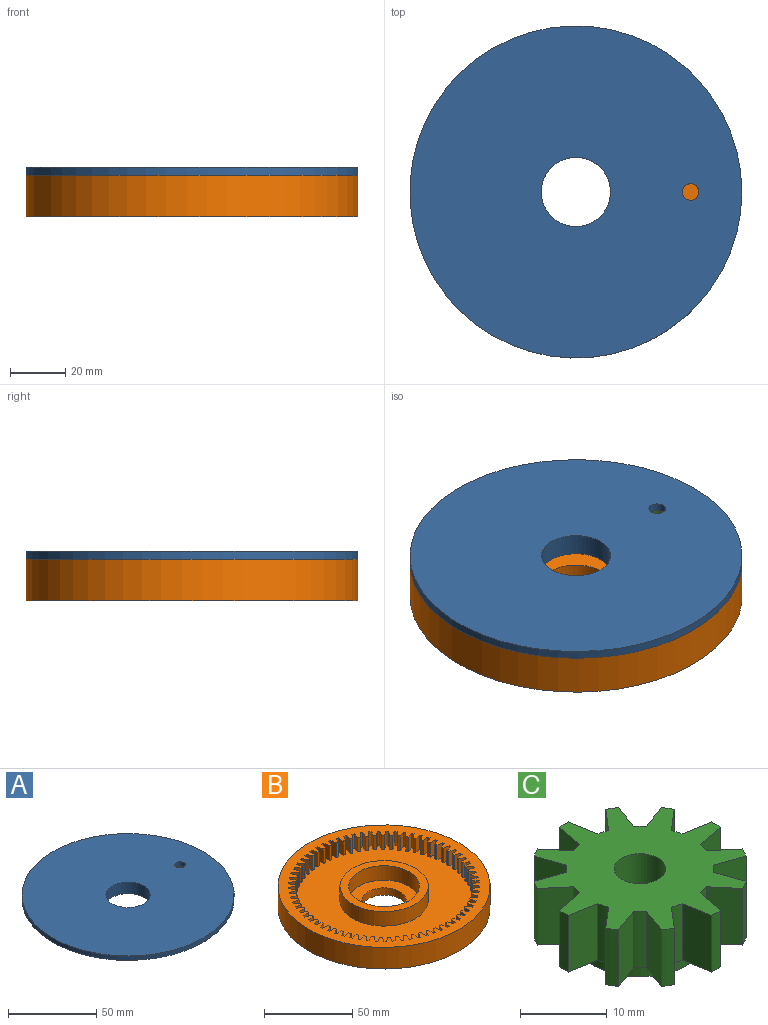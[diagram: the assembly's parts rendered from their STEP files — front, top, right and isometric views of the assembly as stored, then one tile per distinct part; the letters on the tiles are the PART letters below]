
ASSEMBLY  parts=3 mates=2
PART A: 7 faces, bbox 120x120x8 mm
  f0: cylinder r=19.5mm len=39mm, axis (0,0,-1), area 612.6mm2, adj f1,f4
  f1: plane 39x39mm, normal (0,0,-1), area 703.7mm2, adj f0,f5
  f2: cylinder r=60mm len=120mm, axis (0,0,-1), area 1131mm2, adj f3,f4
  f3: plane 120x120mm, normal (0,0,1), area 10790.6mm2, adj f2,f5,f6
  f4: plane 120x120mm, normal (0,0,-1), area 10086.9mm2, adj f0,f2,f6
  f5: cylinder r=12.5mm len=25mm, axis (0,0,1), area 628.3mm2, adj f1,f3
  f6: cylinder r=3mm len=6mm, axis (0,0,1), area 56.5mm2, adj f3,f4
PART B: 285 faces, bbox 120x120x15 mm
  f0: cylinder r=50mm len=10mm, axis (0,0,-1), area 15.5mm2, adj f69,f71,f277,f282
  f1: cylinder r=50mm len=10mm, axis (0,0,-1), area 15.5mm2, adj f69,f71,f274,f279
  f2: cylinder r=50mm len=10mm, axis (0,0,-1), area 15.5mm2, adj f69,f71,f271,f276
  f3: cylinder r=50mm len=10mm, axis (0,0,-1), area 15.5mm2, adj f69,f71,f268,f273
  f4: cylinder r=50mm len=10mm, axis (0,0,-1), area 15.5mm2, adj f69,f71,f265,f270
  f5: cylinder r=50mm len=10mm, axis (0,0,-1), area 15.5mm2, adj f69,f71,f262,f267
  f6: cylinder r=50mm len=10mm, axis (0,0,-1), area 15.5mm2, adj f69,f71,f259,f264
  f7: cylinder r=50mm len=10mm, axis (0,0,-1), area 15.5mm2, adj f69,f71,f235,f261
  f8: cylinder r=50mm len=10mm, axis (0,0,-1), area 15.5mm2, adj f69,f71,f247,f258
  f9: cylinder r=50mm len=10mm, axis (0,0,-1), area 15.5mm2, adj f69,f71,f255,f256
  f10: cylinder r=50mm len=10mm, axis (0,0,-1), area 15.5mm2, adj f69,f71,f232,f252
  f11: cylinder r=50mm len=10mm, axis (0,0,-1), area 15.5mm2, adj f69,f71,f249,f250
  f12: cylinder r=50mm len=10mm, axis (0,0,-1), area 15.5mm2, adj f69,f71,f241,f246
  f13: cylinder r=50mm len=10mm, axis (0,0,-1), area 15.5mm2, adj f69,f71,f243,f253
  f14: cylinder r=50mm len=10mm, axis (0,0,-1), area 15.5mm2, adj f69,f71,f240,f244
  f15: cylinder r=50mm len=10mm, axis (0,0,-1), area 15.5mm2, adj f69,f71,f237,f238
  f16: cylinder r=50mm len=10mm, axis (0,0,-1), area 15.5mm2, adj f69,f71,f229,f234
  f17: cylinder r=50mm len=10mm, axis (0,0,-1), area 15.5mm2, adj f69,f71,f226,f231
  f18: cylinder r=50mm len=10mm, axis (0,0,-1), area 15.5mm2, adj f69,f71,f223,f228
  f19: cylinder r=50mm len=10mm, axis (0,0,-1), area 15.5mm2, adj f69,f71,f220,f225
  f20: cylinder r=50mm len=10mm, axis (0,0,-1), area 15.5mm2, adj f69,f71,f217,f222
  f21: cylinder r=50mm len=10mm, axis (0,0,-1), area 15.5mm2, adj f69,f71,f214,f219
  f22: cylinder r=50mm len=10mm, axis (0,0,-1), area 15.5mm2, adj f69,f71,f211,f216
  f23: cylinder r=50mm len=10mm, axis (0,0,-1), area 15.5mm2, adj f69,f71,f208,f213
  f24: cylinder r=50mm len=10mm, axis (0,0,-1), area 15.5mm2, adj f69,f71,f205,f210
  f25: cylinder r=50mm len=10mm, axis (0,0,-1), area 15.5mm2, adj f69,f71,f202,f207
  f26: cylinder r=50mm len=10mm, axis (0,0,-1), area 15.5mm2, adj f69,f71,f199,f204
  f27: cylinder r=50mm len=10mm, axis (0,0,-1), area 15.5mm2, adj f69,f71,f190,f201
  f28: cylinder r=50mm len=10mm, axis (0,0,-1), area 15.5mm2, adj f69,f71,f193,f198
  f29: cylinder r=50mm len=10mm, axis (0,0,-1), area 15.5mm2, adj f69,f71,f94,f195
  f30: cylinder r=50mm len=10mm, axis (0,0,-1), area 15.5mm2, adj f69,f71,f187,f192
  f31: cylinder r=50mm len=10mm, axis (0,0,-1), area 15.5mm2, adj f69,f71,f189,f196
  f32: cylinder r=50mm len=10mm, axis (0,0,-1), area 15.5mm2, adj f69,f71,f181,f186
  f33: cylinder r=50mm len=10mm, axis (0,0,-1), area 15.5mm2, adj f69,f71,f76,f183
  f34: cylinder r=50mm len=10mm, axis (0,0,-1), area 15.5mm2, adj f69,f71,f180,f184
  f35: cylinder r=50mm len=10mm, axis (0,0,-1), area 15.5mm2, adj f69,f71,f177,f178
  f36: cylinder r=50mm len=10mm, axis (0,0,-1), area 15.5mm2, adj f69,f71,f174,f175
  f37: cylinder r=50mm len=10mm, axis (0,0,-1), area 15.5mm2, adj f69,f71,f171,f172
  f38: cylinder r=50mm len=10mm, axis (0,0,-1), area 15.5mm2, adj f69,f71,f168,f169
  f39: cylinder r=50mm len=10mm, axis (0,0,-1), area 15.5mm2, adj f69,f71,f164,f166
  f40: cylinder r=50mm len=10mm, axis (0,0,-1), area 15.5mm2, adj f69,f71,f162,f165
  f41: cylinder r=50mm len=10mm, axis (0,0,-1), area 15.5mm2, adj f69,f71,f159,f160
  f42: cylinder r=50mm len=10mm, axis (0,0,-1), area 15.5mm2, adj f69,f71,f156,f157
  f43: cylinder r=50mm len=10mm, axis (0,0,-1), area 15.5mm2, adj f69,f71,f153,f154
  f44: cylinder r=50mm len=10mm, axis (0,0,-1), area 15.5mm2, adj f69,f71,f142,f150
  f45: cylinder r=50mm len=10mm, axis (0,0,-1), area 15.5mm2, adj f69,f71,f147,f148
  f46: cylinder r=50mm len=10mm, axis (0,0,-1), area 15.5mm2, adj f69,f71,f139,f144
  f47: cylinder r=50mm len=10mm, axis (0,0,-1), area 15.5mm2, adj f69,f71,f141,f151
  f48: cylinder r=50mm len=10mm, axis (0,0,-1), area 15.5mm2, adj f69,f71,f133,f138
  f49: cylinder r=50mm len=10mm, axis (0,0,-1), area 15.5mm2, adj f69,f71,f127,f135
  f50: cylinder r=50mm len=10mm, axis (0,0,-1), area 15.5mm2, adj f69,f71,f132,f145
  f51: cylinder r=50mm len=10mm, axis (0,0,-1), area 15.5mm2, adj f69,f71,f129,f130
  f52: cylinder r=50mm len=10mm, axis (0,0,-1), area 15.5mm2, adj f69,f71,f126,f136
  f53: cylinder r=50mm len=10mm, axis (0,0,-1), area 15.5mm2, adj f69,f71,f123,f124
  f54: cylinder r=50mm len=10mm, axis (0,0,-1), area 15.5mm2, adj f69,f71,f120,f121
  f55: cylinder r=50mm len=10mm, axis (0,0,-1), area 15.5mm2, adj f69,f71,f117,f118
  f56: cylinder r=50mm len=10mm, axis (0,0,-1), area 15.5mm2, adj f69,f71,f114,f115
  f57: cylinder r=50mm len=10mm, axis (0,0,-1), area 15.5mm2, adj f69,f71,f111,f112
  f58: cylinder r=50mm len=10mm, axis (0,0,-1), area 15.5mm2, adj f69,f71,f108,f109
  f59: cylinder r=50mm len=10mm, axis (0,0,-1), area 15.5mm2, adj f69,f71,f105,f106
  f60: cylinder r=50mm len=10mm, axis (0,0,-1), area 15.5mm2, adj f69,f71,f102,f103
  f61: cylinder r=50mm len=10mm, axis (0,0,-1), area 15.5mm2, adj f69,f71,f99,f100
  f62: cylinder r=50mm len=10mm, axis (0,0,-1), area 15.5mm2, adj f69,f71,f91,f96
  f63: cylinder r=50mm len=10mm, axis (0,0,-1), area 15.5mm2, adj f69,f71,f93,f97
  f64: cylinder r=50mm len=10mm, axis (0,0,-1), area 15.5mm2, adj f69,f71,f82,f90
  f65: cylinder r=50mm len=10mm, axis (0,0,-1), area 15.5mm2, adj f69,f71,f87,f88
  f66: cylinder r=50mm len=10mm, axis (0,0,-1), area 15.5mm2, adj f69,f71,f79,f84
  f67: cylinder r=50mm len=10mm, axis (0,0,-1), area 15.5mm2, adj f69,f71,f81,f280
  f68: cylinder r=50mm len=10mm, axis (0,0,-1), area 15.5mm2, adj f69,f71,f78,f85
  f69: plane 120x120mm, normal (0,0,1), area 2834.4mm2, adj f0,f1,f2,f3,f4,f5,f6,f7
  f70: plane 120x120mm, normal (0,0,-1), area 10818.9mm2, adj f283,f284
  f71: plane 108.01x107.98mm, normal (0,0,1), area 6511.9mm2, adj f0,f1,f2,f3,f4,f5,f6,f7
  f72: cylinder r=20mm len=40mm, axis (0,0,-1), area 1256.6mm2, adj f74,f75
  f73: cylinder r=25mm len=50mm, axis (0,0,-1), area 1570.8mm2, adj f71,f74
  f74: plane 50x50mm, normal (0,0,1), area 706.9mm2, adj f72,f73
  f75: plane 40x40mm, normal (0,0,1), area 765.8mm2, adj f72,f283
  f76: plane 10x3.24mm, normal (-0.61,-0.79,0), area 40.9mm2, adj f33,f69,f71,f77
  f77: plane 10x1.12mm, normal (0.67,-0.75,0), area 15mm2, adj f69,f71,f76,f78
  f78: plane 10x3.5mm, normal (0.86,0.52,0), area 40.9mm2, adj f68,f69,f71,f77
  f79: plane 10x3.92mm, normal (-0.29,-0.96,0), area 40.9mm2, adj f66,f69,f71,f80
  f80: plane 10x1.33mm, normal (0.89,-0.46,0), area 15mm2, adj f69,f71,f79,f81
  f81: plane 10x3.23mm, normal (0.62,0.79,0), area 40.9mm2, adj f67,f69,f71,f80
  f82: plane 10x3.79mm, normal (-0.38,-0.93,0), area 40.9mm2, adj f64,f69,f71,f83
  f83: plane 10x1.26mm, normal (0.84,-0.54,0), area 15mm2, adj f69,f71,f82,f84
  f84: plane 10x2.98mm, normal (0.68,0.73,0), area 40.9mm2, adj f66,f69,f71,f83
  f85: plane 10x3.45mm, normal (-0.54,-0.84,0), area 40.9mm2, adj f68,f69,f71,f86
  f86: plane 10x1.1mm, normal (0.73,-0.68,0), area 15mm2, adj f69,f71,f85,f87
  f87: plane 10x3.29mm, normal (0.8,0.59,0), area 40.9mm2, adj f65,f69,f71,f86
  f88: plane 10x3.64mm, normal (-0.46,-0.89,0), area 40.9mm2, adj f65,f69,f71,f89
  f89: plane 10x1.19mm, normal (0.79,-0.61,0), area 15mm2, adj f69,f71,f88,f90
  f90: plane 10x3.06mm, normal (0.75,0.66,0), area 40.9mm2, adj f64,f69,f71,f89
  f91: plane 10x3.86mm, normal (0.33,0.94,0), area 40.9mm2, adj f62,f69,f71,f92
  f92: plane 10x1.3mm, normal (-0.87,0.5,0), area 15mm2, adj f69,f71,f91,f93
  f93: plane 10x3.11mm, normal (-0.65,-0.76,0), area 40.9mm2, adj f63,f69,f71,f92
  f94: plane 10x3.72mm, normal (0.42,0.91,0), area 40.9mm2, adj f29,f69,f71,f95
  f95: plane 10x1.23mm, normal (-0.82,0.58,0), area 15mm2, adj f69,f71,f94,f96
  f96: plane 10x2.93mm, normal (-0.72,-0.7,0), area 40.9mm2, adj f62,f69,f71,f95
  f97: plane 10x3.97mm, normal (0.25,0.97,0), area 40.9mm2, adj f63,f69,f71,f98
  f98: plane 10x1.36mm, normal (-0.91,0.42,0), area 15mm2, adj f69,f71,f97,f99
  f99: plane 10x3.34mm, normal (-0.58,-0.82,0), area 40.9mm2, adj f61,f69,f71,f98
  f100: plane 10x4.04mm, normal (0.16,0.99,0), area 40.9mm2, adj f61,f69,f71,f101
  f101: plane 10x1.41mm, normal (-0.94,0.33,0), area 15mm2, adj f69,f71,f100,f102
  f102: plane 10x3.54mm, normal (-0.5,-0.86,0), area 40.9mm2, adj f60,f69,f71,f101
  f103: plane 10x4.08mm, normal (0.07,1,0), area 40.9mm2, adj f60,f69,f71,f104
  f104: plane 10x1.45mm, normal (-0.97,0.25,0), area 15mm2, adj f69,f71,f103,f105
  f105: plane 10x3.71mm, normal (-0.42,-0.91,0), area 40.9mm2, adj f59,f69,f71,f104
  f106: plane 10x4.09mm, normal (-0.02,1,0), area 40.9mm2, adj f59,f69,f71,f107
  f107: plane 10x1.48mm, normal (-0.99,0.16,0), area 15mm2, adj f69,f71,f106,f108
  f108: plane 10x3.85mm, normal (-0.34,-0.94,0), area 40.9mm2, adj f58,f69,f71,f107
  f109: plane 10x4.06mm, normal (-0.12,0.99,0), area 40.9mm2, adj f58,f69,f71,f110
  f110: plane 10x1.5mm, normal (-1,0.07,0), area 15mm2, adj f69,f71,f109,f111
  f111: plane 10x3.96mm, normal (-0.25,-0.97,0), area 40.9mm2, adj f57,f69,f71,f110
  f112: plane 10x4mm, normal (-0.21,0.98,0), area 40.9mm2, adj f57,f69,f71,f113
  f113: plane 10x1.5mm, normal (-1,-0.02,0), area 15mm2, adj f69,f71,f112,f114
  f114: plane 10x4.04mm, normal (-0.16,-0.99,0), area 40.9mm2, adj f56,f69,f71,f113
  f115: plane 10x3.91mm, normal (-0.29,0.96,0), area 40.9mm2, adj f56,f69,f71,f116
  f116: plane 10x1.49mm, normal (-0.99,-0.11,0), area 15mm2, adj f69,f71,f115,f117
  f117: plane 10x4.08mm, normal (-0.07,-1,0), area 40.9mm2, adj f55,f69,f71,f116
  f118: plane 10x3.79mm, normal (-0.38,0.93,0), area 40.9mm2, adj f55,f69,f71,f119
  f119: plane 10x1.47mm, normal (-0.98,-0.2,0), area 15mm2, adj f69,f71,f118,f120
  f120: plane 10x4.09mm, normal (0.02,-1,0), area 40.9mm2, adj f54,f69,f71,f119
  f121: plane 10x3.63mm, normal (-0.46,0.89,0), area 40.9mm2, adj f54,f69,f71,f122
  f122: plane 10x1.43mm, normal (-0.96,-0.29,0), area 15mm2, adj f69,f71,f121,f123
  f123: plane 10x4.07mm, normal (0.11,-0.99,0), area 40.9mm2, adj f53,f69,f71,f122
  f124: plane 10x3.44mm, normal (-0.54,0.84,0), area 40.9mm2, adj f53,f69,f71,f125
  f125: plane 10x1.39mm, normal (-0.93,-0.38,0), area 15mm2, adj f69,f71,f124,f126
  f126: plane 10x4.01mm, normal (0.2,-0.98,0), area 40.9mm2, adj f52,f69,f71,f125
  f127: plane 10x3.06mm, normal (-0.75,0.66,0), area 40.9mm2, adj f49,f69,f71,f128
  f128: plane 10x1.19mm, normal (-0.79,-0.61,0), area 15mm2, adj f69,f71,f127,f129
  f129: plane 10x3.64mm, normal (0.46,-0.89,0), area 40.9mm2, adj f51,f69,f71,f128
  f130: plane 10x3.29mm, normal (-0.8,0.59,0), area 40.9mm2, adj f51,f69,f71,f131
  f131: plane 10x1.1mm, normal (-0.73,-0.68,0), area 15mm2, adj f69,f71,f130,f132
  f132: plane 10x3.45mm, normal (0.54,-0.84,0), area 40.9mm2, adj f50,f69,f71,f131
  f133: plane 10x2.98mm, normal (-0.68,0.73,0), area 40.9mm2, adj f48,f69,f71,f134
  f134: plane 10x1.26mm, normal (-0.84,-0.54,0), area 15mm2, adj f69,f71,f133,f135
  f135: plane 10x3.79mm, normal (0.38,-0.93,0), area 40.9mm2, adj f49,f69,f71,f134
  f136: plane 10x3.23mm, normal (-0.62,0.79,0), area 40.9mm2, adj f52,f69,f71,f137
  f137: plane 10x1.33mm, normal (-0.89,-0.46,0), area 15mm2, adj f69,f71,f136,f138
  f138: plane 10x3.92mm, normal (0.29,-0.96,0), area 40.9mm2, adj f48,f69,f71,f137
  f139: plane 10x3.94mm, normal (-0.96,0.27,0), area 40.9mm2, adj f46,f69,f71,f140
  f140: plane 10x1.35mm, normal (-0.44,-0.9,0), area 15mm2, adj f69,f71,f139,f141
  f141: plane 10x3.28mm, normal (0.8,-0.6,0), area 40.9mm2, adj f47,f69,f71,f140
  f142: plane 10x3.83mm, normal (-0.94,0.35,0), area 40.9mm2, adj f44,f69,f71,f143
  f143: plane 10x1.28mm, normal (-0.52,-0.85,0), area 15mm2, adj f69,f71,f142,f144
  f144: plane 10x3.05mm, normal (0.74,-0.67,0), area 40.9mm2, adj f46,f69,f71,f143
  f145: plane 10x3.5mm, normal (-0.86,0.52,0), area 40.9mm2, adj f50,f69,f71,f146
  f146: plane 10x1.12mm, normal (-0.67,-0.75,0), area 15mm2, adj f69,f71,f145,f147
  f147: plane 10x3.24mm, normal (0.61,-0.79,0), area 40.9mm2, adj f45,f69,f71,f146
  f148: plane 10x3.68mm, normal (-0.9,0.44,0), area 40.9mm2, adj f45,f69,f71,f149
  f149: plane 10x1.21mm, normal (-0.6,-0.8,0), area 15mm2, adj f69,f71,f148,f150
  f150: plane 10x3mm, normal (0.68,-0.73,0), area 40.9mm2, adj f44,f69,f71,f149
  f151: plane 10x4.03mm, normal (-0.98,0.18,0), area 40.9mm2, adj f47,f69,f71,f152
  f152: plane 10x1.4mm, normal (-0.36,-0.93,0), area 15mm2, adj f69,f71,f151,f153
  f153: plane 10x3.49mm, normal (0.85,-0.52,0), area 40.9mm2, adj f43,f69,f71,f152
  f154: plane 10x4.08mm, normal (-1,0.09,0), area 40.9mm2, adj f43,f69,f71,f155
  f155: plane 10x1.44mm, normal (-0.27,-0.96,0), area 15mm2, adj f69,f71,f154,f156
  f156: plane 10x3.67mm, normal (0.9,-0.44,0), area 40.9mm2, adj f42,f69,f71,f155
  f157: plane 10x4.09mm, normal (-1,0,0), area 40.9mm2, adj f42,f69,f71,f158
  f158: plane 10x1.48mm, normal (-0.18,-0.98,0), area 15mm2, adj f69,f71,f157,f159
  f159: plane 10x3.82mm, normal (0.93,-0.36,0), area 40.9mm2, adj f41,f69,f71,f158
  f160: plane 10x4.07mm, normal (-1,-0.09,0), area 40.9mm2, adj f41,f69,f71,f161
  f161: plane 10x1.49mm, normal (-0.09,-1,0), area 15mm2, adj f69,f71,f160,f162
  f162: plane 10x3.94mm, normal (0.96,-0.27,0), area 40.9mm2, adj f40,f69,f71,f161
  f163: plane 10x1.5mm, normal (0,-1,0), area 15mm2, adj f69,f71,f164,f165
  f164: plane 10x4.02mm, normal (0.98,-0.18,0), area 40.9mm2, adj f39,f69,f71,f163
  f165: plane 10x4.02mm, normal (-0.98,-0.18,0), area 40.9mm2, adj f40,f69,f71,f163
  f166: plane 10x3.94mm, normal (-0.96,-0.27,0), area 40.9mm2, adj f39,f69,f71,f167
  f167: plane 10x1.49mm, normal (0.09,-1,0), area 15mm2, adj f69,f71,f166,f168
  f168: plane 10x4.07mm, normal (1,-0.09,0), area 40.9mm2, adj f38,f69,f71,f167
  f169: plane 10x3.82mm, normal (-0.93,-0.36,0), area 40.9mm2, adj f38,f69,f71,f170
  f170: plane 10x1.48mm, normal (0.18,-0.98,0), area 15mm2, adj f69,f71,f169,f171
  f171: plane 10x4.09mm, normal (1,0,0), area 40.9mm2, adj f37,f69,f71,f170
  f172: plane 10x3.67mm, normal (-0.9,-0.44,0), area 40.9mm2, adj f37,f69,f71,f173
  f173: plane 10x1.44mm, normal (0.27,-0.96,0), area 15mm2, adj f69,f71,f172,f174
  f174: plane 10x4.08mm, normal (1,0.09,0), area 40.9mm2, adj f36,f69,f71,f173
  f175: plane 10x3.49mm, normal (-0.85,-0.52,0), area 40.9mm2, adj f36,f69,f71,f176
  f176: plane 10x1.4mm, normal (0.36,-0.93,0), area 15mm2, adj f69,f71,f175,f177
  f177: plane 10x4.03mm, normal (0.98,0.18,0), area 40.9mm2, adj f35,f69,f71,f176
  f178: plane 10x3.28mm, normal (-0.8,-0.6,0), area 40.9mm2, adj f35,f69,f71,f179
  f179: plane 10x1.35mm, normal (0.44,-0.9,0), area 15mm2, adj f69,f71,f178,f180
  f180: plane 10x3.94mm, normal (0.96,0.27,0), area 40.9mm2, adj f34,f69,f71,f179
  f181: plane 10x3mm, normal (-0.68,-0.73,0), area 40.9mm2, adj f32,f69,f71,f182
  f182: plane 10x1.21mm, normal (0.6,-0.8,0), area 15mm2, adj f69,f71,f181,f183
  f183: plane 10x3.68mm, normal (0.9,0.44,0), area 40.9mm2, adj f33,f69,f71,f182
  f184: plane 10x3.05mm, normal (-0.74,-0.67,0), area 40.9mm2, adj f34,f69,f71,f185
  f185: plane 10x1.28mm, normal (0.52,-0.85,0), area 15mm2, adj f69,f71,f184,f186
  f186: plane 10x3.83mm, normal (0.94,0.35,0), area 40.9mm2, adj f32,f69,f71,f185
  f187: plane 10x3.12mm, normal (0.65,0.76,0), area 40.9mm2, adj f30,f69,f71,f188
  f188: plane 10x1.16mm, normal (-0.63,0.78,0), area 15mm2, adj f69,f71,f187,f189
  f189: plane 10x3.59mm, normal (-0.88,-0.48,0), area 40.9mm2, adj f31,f69,f71,f188
  f190: plane 10x2.92mm, normal (0.71,0.7,0), area 40.9mm2, adj f27,f69,f71,f191
  f191: plane 10x1.25mm, normal (-0.56,0.83,0), area 15mm2, adj f69,f71,f190,f192
  f192: plane 10x3.76mm, normal (-0.92,-0.4,0), area 40.9mm2, adj f30,f69,f71,f191
  f193: plane 10x3.55mm, normal (0.5,0.87,0), area 40.9mm2, adj f28,f69,f71,f194
  f194: plane 10x1.14mm, normal (-0.76,0.65,0), area 15mm2, adj f69,f71,f193,f195
  f195: plane 10x3.18mm, normal (-0.78,-0.63,0), area 40.9mm2, adj f29,f69,f71,f194
  f196: plane 10x3.35mm, normal (0.57,0.82,0), area 40.9mm2, adj f31,f69,f71,f197
  f197: plane 10x1.07mm, normal (-0.7,0.72,0), area 15mm2, adj f69,f71,f196,f198
  f198: plane 10x3.4mm, normal (-0.83,-0.56,0), area 40.9mm2, adj f28,f69,f71,f197
  f199: plane 10x3.17mm, normal (0.77,0.63,0), area 40.9mm2, adj f26,f69,f71,f200
  f200: plane 10x1.32mm, normal (-0.48,0.88,0), area 15mm2, adj f69,f71,f199,f201
  f201: plane 10x3.89mm, normal (-0.95,-0.31,0), area 40.9mm2, adj f27,f69,f71,f200
  f202: plane 10x3.39mm, normal (0.83,0.56,0), area 40.9mm2, adj f25,f69,f71,f203
  f203: plane 10x1.38mm, normal (-0.4,0.92,0), area 15mm2, adj f69,f71,f202,f204
  f204: plane 10x3.99mm, normal (-0.97,-0.22,0), area 40.9mm2, adj f26,f69,f71,f203
  f205: plane 10x3.59mm, normal (0.88,0.48,0), area 40.9mm2, adj f24,f69,f71,f206
  f206: plane 10x1.42mm, normal (-0.31,0.95,0), area 15mm2, adj f69,f71,f205,f207
  f207: plane 10x4.06mm, normal (-0.99,-0.13,0), area 40.9mm2, adj f25,f69,f71,f206
  f208: plane 10x3.75mm, normal (0.92,0.4,0), area 40.9mm2, adj f23,f69,f71,f209
  f209: plane 10x1.46mm, normal (-0.23,0.97,0), area 15mm2, adj f69,f71,f208,f210
  f210: plane 10x4.09mm, normal (-1,-0.04,0), area 40.9mm2, adj f24,f69,f71,f209
  f211: plane 10x3.88mm, normal (0.95,0.32,0), area 40.9mm2, adj f22,f69,f71,f212
  f212: plane 10x1.49mm, normal (-0.14,0.99,0), area 15mm2, adj f69,f71,f211,f213
  f213: plane 10x4.09mm, normal (-1,0.05,0), area 40.9mm2, adj f23,f69,f71,f212
  f214: plane 10x3.98mm, normal (0.97,0.23,0), area 40.9mm2, adj f21,f69,f71,f215
  f215: plane 10x1.5mm, normal (-0.05,1,0), area 15mm2, adj f69,f71,f214,f216
  f216: plane 10x4.05mm, normal (-0.99,0.14,0), area 40.9mm2, adj f22,f69,f71,f215
  f217: plane 10x4.05mm, normal (0.99,0.14,0), area 40.9mm2, adj f20,f69,f71,f218
  f218: plane 10x1.5mm, normal (0.05,1,0), area 15mm2, adj f69,f71,f217,f219
  f219: plane 10x3.98mm, normal (-0.97,0.23,0), area 40.9mm2, adj f21,f69,f71,f218
  f220: plane 10x4.09mm, normal (1,0.05,0), area 40.9mm2, adj f19,f69,f71,f221
  f221: plane 10x1.49mm, normal (0.14,0.99,0), area 15mm2, adj f69,f71,f220,f222
  f222: plane 10x3.88mm, normal (-0.95,0.32,0), area 40.9mm2, adj f20,f69,f71,f221
  f223: plane 10x4.09mm, normal (1,-0.04,0), area 40.9mm2, adj f18,f69,f71,f224
  f224: plane 10x1.46mm, normal (0.23,0.97,0), area 15mm2, adj f69,f71,f223,f225
  f225: plane 10x3.75mm, normal (-0.92,0.4,0), area 40.9mm2, adj f19,f69,f71,f224
  f226: plane 10x4.06mm, normal (0.99,-0.13,0), area 40.9mm2, adj f17,f69,f71,f227
  f227: plane 10x1.42mm, normal (0.31,0.95,0), area 15mm2, adj f69,f71,f226,f228
  f228: plane 10x3.59mm, normal (-0.88,0.48,0), area 40.9mm2, adj f18,f69,f71,f227
  f229: plane 10x3.99mm, normal (0.97,-0.22,0), area 40.9mm2, adj f16,f69,f71,f230
  f230: plane 10x1.38mm, normal (0.4,0.92,0), area 15mm2, adj f69,f71,f229,f231
  f231: plane 10x3.39mm, normal (-0.83,0.56,0), area 40.9mm2, adj f17,f69,f71,f230
  f232: plane 10x3.89mm, normal (0.95,-0.31,0), area 40.9mm2, adj f10,f69,f71,f233
  f233: plane 10x1.32mm, normal (0.48,0.88,0), area 15mm2, adj f69,f71,f232,f234
  f234: plane 10x3.17mm, normal (-0.77,0.63,0), area 40.9mm2, adj f16,f69,f71,f233
  f235: plane 10x3.54mm, normal (0.5,-0.86,0), area 40.9mm2, adj f7,f69,f71,f236
  f236: plane 10x1.41mm, normal (0.94,0.33,0), area 15mm2, adj f69,f71,f235,f237
  f237: plane 10x4.04mm, normal (-0.16,0.99,0), area 40.9mm2, adj f15,f69,f71,f236
  f238: plane 10x3.34mm, normal (0.58,-0.82,0), area 40.9mm2, adj f15,f69,f71,f239
  f239: plane 10x1.36mm, normal (0.91,0.42,0), area 15mm2, adj f69,f71,f238,f240
  f240: plane 10x3.97mm, normal (-0.25,0.97,0), area 40.9mm2, adj f14,f69,f71,f239
  f241: plane 10x2.93mm, normal (0.72,-0.7,0), area 40.9mm2, adj f12,f69,f71,f242
  f242: plane 10x1.23mm, normal (0.82,0.58,0), area 15mm2, adj f69,f71,f241,f243
  f243: plane 10x3.72mm, normal (-0.42,0.91,0), area 40.9mm2, adj f13,f69,f71,f242
  f244: plane 10x3.11mm, normal (0.65,-0.76,0), area 40.9mm2, adj f14,f69,f71,f245
  f245: plane 10x1.3mm, normal (0.87,0.5,0), area 15mm2, adj f69,f71,f244,f246
  f246: plane 10x3.86mm, normal (-0.33,0.94,0), area 40.9mm2, adj f12,f69,f71,f245
  f247: plane 10x3.59mm, normal (0.88,-0.48,0), area 40.9mm2, adj f8,f69,f71,f248
  f248: plane 10x1.16mm, normal (0.63,0.78,0), area 15mm2, adj f69,f71,f247,f249
  f249: plane 10x3.12mm, normal (-0.65,0.76,0), area 40.9mm2, adj f11,f69,f71,f248
  f250: plane 10x3.76mm, normal (0.92,-0.4,0), area 40.9mm2, adj f11,f69,f71,f251
  f251: plane 10x1.25mm, normal (0.56,0.83,0), area 15mm2, adj f69,f71,f250,f252
  f252: plane 10x2.92mm, normal (-0.71,0.7,0), area 40.9mm2, adj f10,f69,f71,f251
  f253: plane 10x3.18mm, normal (0.78,-0.63,0), area 40.9mm2, adj f13,f69,f71,f254
  f254: plane 10x1.14mm, normal (0.76,0.65,0), area 15mm2, adj f69,f71,f253,f255
  f255: plane 10x3.55mm, normal (-0.5,0.87,0), area 40.9mm2, adj f9,f69,f71,f254
  f256: plane 10x3.4mm, normal (0.83,-0.56,0), area 40.9mm2, adj f9,f69,f71,f257
  f257: plane 10x1.07mm, normal (0.7,0.72,0), area 15mm2, adj f69,f71,f256,f258
  f258: plane 10x3.35mm, normal (-0.57,0.82,0), area 40.9mm2, adj f8,f69,f71,f257
  f259: plane 10x3.71mm, normal (0.42,-0.91,0), area 40.9mm2, adj f6,f69,f71,f260
  f260: plane 10x1.45mm, normal (0.97,0.25,0), area 15mm2, adj f69,f71,f259,f261
  f261: plane 10x4.08mm, normal (-0.07,1,0), area 40.9mm2, adj f7,f69,f71,f260
  f262: plane 10x3.85mm, normal (0.34,-0.94,0), area 40.9mm2, adj f5,f69,f71,f263
  f263: plane 10x1.48mm, normal (0.99,0.16,0), area 15mm2, adj f69,f71,f262,f264
  f264: plane 10x4.09mm, normal (0.02,1,0), area 40.9mm2, adj f6,f69,f71,f263
  f265: plane 10x3.96mm, normal (0.25,-0.97,0), area 40.9mm2, adj f4,f69,f71,f266
  f266: plane 10x1.5mm, normal (1,0.07,0), area 15mm2, adj f69,f71,f265,f267
  f267: plane 10x4.06mm, normal (0.12,0.99,0), area 40.9mm2, adj f5,f69,f71,f266
  f268: plane 10x4.04mm, normal (0.16,-0.99,0), area 40.9mm2, adj f3,f69,f71,f269
  f269: plane 10x1.5mm, normal (1,-0.02,0), area 15mm2, adj f69,f71,f268,f270
  f270: plane 10x4mm, normal (0.21,0.98,0), area 40.9mm2, adj f4,f69,f71,f269
  f271: plane 10x4.08mm, normal (0.07,-1,0), area 40.9mm2, adj f2,f69,f71,f272
  f272: plane 10x1.49mm, normal (0.99,-0.11,0), area 15mm2, adj f69,f71,f271,f273
  f273: plane 10x3.91mm, normal (0.29,0.96,0), area 40.9mm2, adj f3,f69,f71,f272
  f274: plane 10x4.09mm, normal (-0.02,-1,0), area 40.9mm2, adj f1,f69,f71,f275
  f275: plane 10x1.47mm, normal (0.98,-0.2,0), area 15mm2, adj f69,f71,f274,f276
  f276: plane 10x3.79mm, normal (0.38,0.93,0), area 40.9mm2, adj f2,f69,f71,f275
  f277: plane 10x4.07mm, normal (-0.11,-0.99,0), area 40.9mm2, adj f0,f69,f71,f278
  f278: plane 10x1.43mm, normal (0.96,-0.29,0), area 15mm2, adj f69,f71,f277,f279
  f279: plane 10x3.63mm, normal (0.46,0.89,0), area 40.9mm2, adj f1,f69,f71,f278
  f280: plane 10x4.01mm, normal (-0.2,-0.98,0), area 40.9mm2, adj f67,f69,f71,f281
  f281: plane 10x1.39mm, normal (0.93,-0.38,0), area 15mm2, adj f69,f71,f280,f282
  f282: plane 10x3.44mm, normal (0.54,0.84,0), area 40.9mm2, adj f0,f69,f71,f281
  f283: cylinder r=12.5mm len=25mm, axis (0,0,1), area 392.7mm2, adj f70,f75
  f284: cylinder r=60mm len=120mm, axis (0,0,1), area 5654.9mm2, adj f69,f70
PART C: 53 faces, bbox 25x25x10 mm
  f0: cylinder r=12.5mm len=8mm, axis (0,0,-1), area 12.1mm2, adj f11,f12,f44,f51
  f1: cylinder r=12.5mm len=8mm, axis (0,0,-1), area 12.1mm2, adj f11,f12,f48,f50
  f2: cylinder r=12.5mm len=8mm, axis (0,0,-1), area 12.1mm2, adj f11,f12,f41,f45
  f3: cylinder r=12.5mm len=8mm, axis (0,0,-1), area 12.1mm2, adj f11,f12,f17,f42
  f4: cylinder r=12.5mm len=8mm, axis (0,0,-1), area 12.1mm2, adj f11,f12,f35,f39
  f5: cylinder r=12.5mm len=8mm, axis (0,0,-1), area 12.1mm2, adj f11,f12,f29,f36
  f6: cylinder r=12.5mm len=8mm, axis (0,0,-1), area 12.1mm2, adj f11,f12,f32,f47
  f7: cylinder r=12.5mm len=8mm, axis (0,0,-1), area 12.1mm2, adj f11,f12,f30,f34
  f8: cylinder r=12.5mm len=8mm, axis (0,0,-1), area 12.1mm2, adj f11,f12,f23,f27
  f9: cylinder r=12.5mm len=8mm, axis (0,0,-1), area 12.1mm2, adj f11,f12,f24,f38
  f10: cylinder r=12.5mm len=8mm, axis (0,0,-1), area 12.1mm2, adj f11,f12,f21,f26
  f11: plane 25x25mm, normal (0,0,1), area 307mm2, adj f0,f1,f2,f3,f4,f5,f6,f7
  f12: plane 25x25mm, normal (0,0,-1), area 158.5mm2, adj f0,f1,f2,f3,f4,f5,f6,f7
  f13: cylinder r=12.5mm len=8mm, axis (0,0,-1), area 12.1mm2, adj f11,f12,f18,f20
  f14: cylinder r=3mm len=10mm, axis (0,0,-1), area 188.5mm2, adj f11,f16
  f15: cylinder r=7.5mm len=15mm, axis (0,0,1), area 94.2mm2, adj f12,f16
  f16: plane 15x15mm, normal (0,0,-1), area 148.4mm2, adj f14,f15
  f17: plane 8x3.93mm, normal (0.34,-0.94,0), area 33.4mm2, adj f3,f11,f12,f19
  f18: plane 8x3.93mm, normal (-0.94,0.34,0), area 33.4mm2, adj f11,f12,f13,f19
  f19: cylinder r=8.5mm len=8mm, axis (0,0,1), area 11.5mm2, adj f11,f12,f17,f18
  f20: plane 8x3.19mm, normal (0.76,-0.65,0), area 33.4mm2, adj f11,f12,f13,f22
  f21: plane 8x4.11mm, normal (-0.98,-0.18,0), area 33.4mm2, adj f10,f11,f12,f22
  f22: cylinder r=8.5mm len=8mm, axis (0,0,1), area 11.5mm2, adj f11,f12,f20,f21
  f23: plane 8x3.93mm, normal (0.94,0.34,0), area 33.4mm2, adj f8,f11,f12,f25
  f24: plane 8x3.93mm, normal (-0.34,-0.94,0), area 33.4mm2, adj f9,f11,f12,f25
  f25: cylinder r=8.5mm len=8mm, axis (0,0,1), area 11.5mm2, adj f11,f12,f23,f24
  f26: plane 8x4.11mm, normal (0.98,-0.18,0), area 33.4mm2, adj f10,f11,f12,f28
  f27: plane 8x3.19mm, normal (-0.76,-0.65,0), area 33.4mm2, adj f8,f11,f12,f28
  f28: cylinder r=8.5mm len=8mm, axis (0,0,1), area 11.5mm2, adj f11,f12,f26,f27
  f29: plane 8x3.93mm, normal (-0.34,0.94,0), area 33.4mm2, adj f5,f11,f12,f31
  f30: plane 8x3.93mm, normal (0.94,-0.34,0), area 33.4mm2, adj f7,f11,f12,f31
  f31: cylinder r=8.5mm len=8mm, axis (0,0,1), area 11.5mm2, adj f11,f12,f29,f30
  f32: plane 8x4.11mm, normal (0.98,0.18,0), area 33.4mm2, adj f6,f11,f12,f33
  f33: cylinder r=8.5mm len=8mm, axis (0,0,1), area 11.5mm2, adj f11,f12,f32,f34
  f34: plane 8x3.19mm, normal (-0.76,0.65,0), area 33.4mm2, adj f7,f11,f12,f33
  f35: plane 8x4.11mm, normal (0.18,0.98,0), area 33.4mm2, adj f4,f11,f12,f37
  f36: plane 8x3.19mm, normal (0.65,-0.76,0), area 33.4mm2, adj f5,f11,f12,f37
  f37: cylinder r=8.5mm len=8mm, axis (0,0,1), area 11.5mm2, adj f11,f12,f35,f36
  f38: plane 8x3.19mm, normal (0.65,0.76,0), area 33.4mm2, adj f9,f11,f12,f40
  f39: plane 8x4.11mm, normal (0.18,-0.98,0), area 33.4mm2, adj f4,f11,f12,f40
  f40: cylinder r=8.5mm len=8mm, axis (0,0,1), area 11.5mm2, adj f11,f12,f38,f39
  f41: plane 8x4.11mm, normal (-0.18,-0.98,0), area 33.4mm2, adj f2,f11,f12,f43
  f42: plane 8x3.19mm, normal (-0.65,0.76,0), area 33.4mm2, adj f3,f11,f12,f43
  f43: cylinder r=8.5mm len=8mm, axis (0,0,1), area 11.5mm2, adj f11,f12,f41,f42
  f44: plane 8x3.19mm, normal (-0.65,-0.76,0), area 33.4mm2, adj f0,f11,f12,f46
  f45: plane 8x4.11mm, normal (-0.18,0.98,0), area 33.4mm2, adj f2,f11,f12,f46
  f46: cylinder r=8.5mm len=8mm, axis (0,0,1), area 11.5mm2, adj f11,f12,f44,f45
  f47: plane 8x4.11mm, normal (-0.98,0.18,0), area 33.4mm2, adj f6,f11,f12,f49
  f48: plane 8x3.19mm, normal (0.76,0.65,0), area 33.4mm2, adj f1,f11,f12,f49
  f49: cylinder r=8.5mm len=8mm, axis (0,0,1), area 11.5mm2, adj f11,f12,f47,f48
  f50: plane 8x3.93mm, normal (-0.94,-0.34,0), area 33.4mm2, adj f1,f11,f12,f52
  f51: plane 8x3.93mm, normal (0.34,0.94,0), area 33.4mm2, adj f0,f11,f12,f52
  f52: cylinder r=8.5mm len=8mm, axis (0,0,1), area 11.5mm2, adj f11,f12,f50,f51
PLACE A t=(0.35,0.23,2.54)mm
PLACE B t=(0.35,0.23,-7.46)mm
PLACE C t=(41.85,0.23,-0.46)mm
MATE fastened C.f14 <-> A.f6  axis (0,0,1) through (41.85,0.23,7.54)mm
MATE fastened A.f0 <-> B.f72  axis (0,0,-1) through (0.35,0.23,7.54)mm
